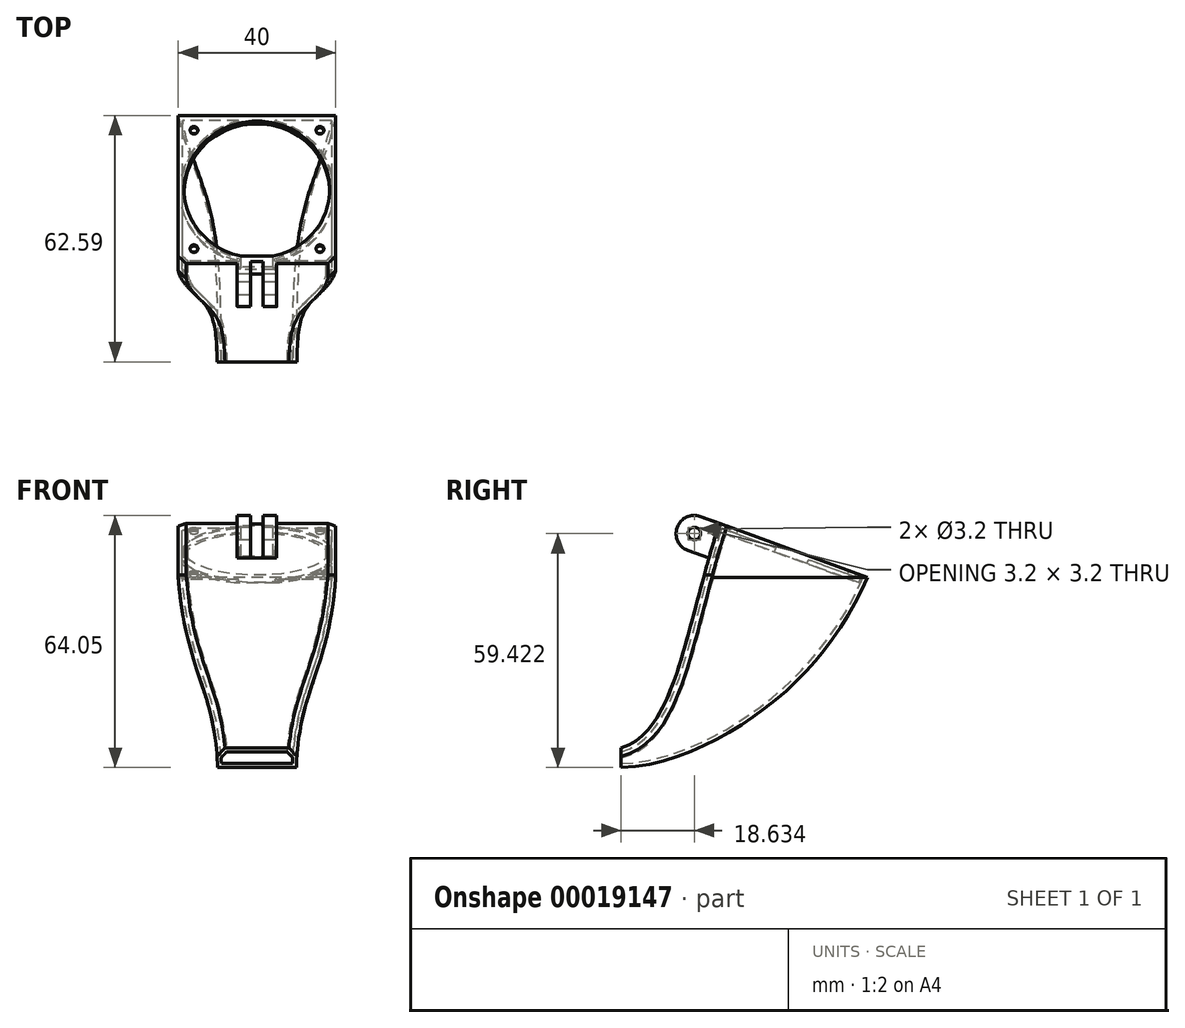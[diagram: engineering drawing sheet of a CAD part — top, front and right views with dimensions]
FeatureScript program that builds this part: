
annotation { "Feature Type Name" : "Feature", "Feature Type Description" : "" }
export const myFeature = defineFeature(function(context is Context, id is Id, definition is map)
    precondition{}
    {
        {
            var Q0;
            Q0=qCreatedBy(makeId("Right.planeOp"),FACE);
            var sketch = newSketch(context, id + "F0", { "sketchPlane" : qUnion([Q0])});
            skLineSegment(sketch, "E0", {"start": v(0, 5) * mm, "end": v(0, 0) * mm});
            skLineSegment(sketch, "E1", {"start": v(62.59, 48.32) * mm, "end": v(25, 62) * mm});
            skFitSpline(sketch, "E2", {"points": [v(62.59, 48.32) * mm, v(0, 0) * mm], "startDerivative": vector(-40.57, -96.87) * mm, "endDerivative": vector(-50.06, 0) * mm});
            skFitSpline(sketch, "E3", {"points": [v(25, 62) * mm, v(0, 5) * mm], "startDerivative": vector(-26.25, -81.63) * mm, "endDerivative": vector(-41.59, -11.88) * mm});
            skSolve(sketch);
        }
        {
            var Q0;
            Q0=qSketchRegion(id+"F0",true);
            extrude(context, id + "F1", {"entities" : qUnion([Q0]), "endBound" : BoundingType.SYMMETRIC, "depth" : 40 * mm});
        }
        {
            var Q0;
            Q0=qCreatedBy(makeId("Front.planeOp"),FACE);
            var sketch = newSketch(context, id + "F2", { "sketchPlane" : qUnion([Q0])});
            skLineSegment(sketch, "E4", {"start": v(10, 0) * mm, "end": v(-10, 0) * mm});
            skLineSegment(sketch, "E5", {"start": v(20, 62) * mm, "end": v(-20, 62) * mm});
            skLineSegment(sketch, "E6", {"start": v(-20, 62) * mm, "end": v(-20, 48.32) * mm});
            skLineSegment(sketch, "E7", {"start": v(20, 62) * mm, "end": v(20, 48.32) * mm});
            skPoint(sketch, "E8", {"position": v(0, 0) * mm});
            skFitSpline(sketch, "E9", {"points": [v(20, 48.32) * mm, v(10, 0) * mm], "startDerivative": vector(-5.16, -71.52) * mm, "endDerivative": vector(-1.89, -60.47) * mm});
            skFitSpline(sketch, "E10.0.MirrorCS", {"points": [v(-20, 48.32) * mm, v(-10, 0) * mm], "startDerivative": vector(5.16, -71.52) * mm, "endDerivative": vector(1.89, -60.47) * mm});
            skSolve(sketch);
        }
        {
            var Q0;
            Q0=qSketchRegion(id+"F2",true);
            var Q1;
            Q1=makeQuery(id+"F1.opExtrude","SWEPT_FACE",FACE,{"disambiguationData":[OSD([sQuery(id+"F0.wireOp",EDGE,"E2")])]});
            extrude(context, id + "F3", {"entities" : qUnion([Q0]), "operationType" : NewBodyOperationType.INTERSECT, "endBound" : BoundingType.UP_TO_BODY, "oppositeDirection" : true, "endBoundEntityBody" : qUnion([Q1]), "depth" : 25 * mm});
        }
        {
            var Q0;
            Q0=makeQuery(id+"F1.opExtrude","SWEPT_FACE",FACE,{"disambiguationData":[OSD([sQuery(id+"F0.wireOp",EDGE,"E1")])]});
            var sketch = newSketch(context, id + "F4", { "sketchPlane" : qUnion([Q0])});
            skLineSegment(sketch, "E11", {"start": v(20, 2.29) * mm, "end": v(-20, 42.29) * mm, "construction": true});
            skLineSegment(sketch, "E12", {"start": v(-20, 2.29) * mm, "end": v(20, 42.29) * mm, "construction": true});
            skCircle(sketch, "E13", {"center": v(0, 22.29) * mm, "radius": 18.5 * mm});
            skSolve(sketch);
        }
        {
            var Q0;
            Q0=qSketchRegion(id+"F4",true);
            extrude(context, id + "F5", {"entities" : qUnion([Q0]), "operationType" : NewBodyOperationType.REMOVE, "oppositeDirection" : true, "depth" : 2 * mm});
        }
        {
            var Q0;
            Q0=makeQuery(id+"F3.boolean.opBoolean","COPY",EDGE,{"derivedFrom":makeQuery(id+"F3.opExtrude","TWEAK_EDGE",EDGE,{"derivedFrom":[makeQuery(id+"F1.opExtrude","SWEPT_FACE",FACE,{"disambiguationData":[OSD([sQuery(id+"F0.wireOp",EDGE,"E2")])]}),makeQuery(id+"F2.imprint","IMPRINT",EDGE,{"derivedFrom":sQuery(id+"F2.wireOp",EDGE,"E9")})]})});
            var Q1;
            Q1=makeQuery(id+"F3.boolean.opBoolean","INTERSECT",EDGE,{"derivedFrom":[makeQuery(id+"F1.opExtrude","SWEPT_FACE",FACE,{"disambiguationData":[OSD([sQuery(id+"F0.wireOp",EDGE,"E3")])]}),makeQuery(id+"F3.opExtrude","SWEPT_FACE",FACE,{"disambiguationData":[OSD([sQuery(id+"F2.wireOp",EDGE,"E9")])]})]});
            var Q2;
            Q2=makeQuery(id+"F1.opExtrude","CAP_EDGE",EDGE,{"disambiguationData":[OSD([sQuery(id+"F0.wireOp",EDGE,"E3")])],"isStart":false});
            var Q3;
            Q3=makeQuery(id+"F3.boolean.opBoolean","INTERSECT",EDGE,{"derivedFrom":[makeQuery(id+"F1.opExtrude","SWEPT_FACE",FACE,{"disambiguationData":[OSD([sQuery(id+"F0.wireOp",EDGE,"E3")])]}),makeQuery(id+"F3.opExtrude","SWEPT_FACE",FACE,{"disambiguationData":[OSD([sQuery(id+"F2.wireOp",EDGE,"E10.0.MirrorCS")])]})]});
            var Q4;
            Q4=makeQuery(id+"F1.opExtrude","CAP_EDGE",EDGE,{"disambiguationData":[OSD([sQuery(id+"F0.wireOp",EDGE,"E3")])],"isStart":true});
            var Q5;
            Q5=makeQuery(id+"F3.boolean.opBoolean","COPY",EDGE,{"derivedFrom":makeQuery(id+"F3.opExtrude","TWEAK_EDGE",EDGE,{"derivedFrom":[makeQuery(id+"F1.opExtrude","SWEPT_FACE",FACE,{"disambiguationData":[OSD([sQuery(id+"F0.wireOp",EDGE,"E2")])]}),makeQuery(id+"F2.imprint","IMPRINT",EDGE,{"derivedFrom":sQuery(id+"F2.wireOp",EDGE,"E10.0.MirrorCS")})]})});
            chamfer(context, id + "F6", {"entities" : qUnion([Q0, Q1, Q2, Q3, Q4, Q5]), "width" : 2 * mm, "tangentPropagation" : true});
        }
        {
            var Q0;
            Q0=makeQuery(id+"F5.boolean.opBoolean","COPY",FACE,{"derivedFrom":makeQuery(id+"F5.opExtrude","CAP_FACE",FACE,{"disambiguationData":[OSD([sQuery(id+"F4.wireOp",EDGE,"E13")])],"isStart":false})});
            var Q1;
            Q1=makeQuery(id+"F1.opExtrude","SWEPT_FACE",FACE,{"disambiguationData":[OSD([sQuery(id+"F0.wireOp",EDGE,"E0")])]});
            shell(context, id + "F7", {"entities" : qUnion([Q0, Q1]), "thickness" : 1 * mm});
        }
        {
            var Q0;
            Q0=makeQuery(id+"F1.opExtrude","SWEPT_FACE",FACE,{"disambiguationData":[OSD([sQuery(id+"F0.wireOp",EDGE,"E1")])]});
            var sketch = newSketch(context, id + "F8", { "sketchPlane" : qUnion([Q0])});
            skCircle(sketch, "E14", {"center": v(16, 38.34) * mm, "radius": 1 * mm});
            skCircle(sketch, "E15", {"center": v(-16, 38.34) * mm, "radius": 1 * mm});
            skCircle(sketch, "E16", {"center": v(-16, 6.34) * mm, "radius": 1 * mm});
            skCircle(sketch, "E17", {"center": v(16, 6.34) * mm, "radius": 1 * mm});
            skPoint(sketch, "E18", {"position": v(-20, 22.34) * mm});
            skSolve(sketch);
        }
        {
            var Q0;
            Q0=qSketchRegion(id+"F8",true);
            var Q1;
            Q1=makeQuery(id+"F7.opShell","OFFSET_FACE",FACE,{"disambiguationData":[OSD([sQuery(id+"F0.wireOp",EDGE,"E1")]),OD(1.0)]});
            extrude(context, id + "F9", {"entities" : qUnion([Q0]), "operationType" : NewBodyOperationType.REMOVE, "endBound" : BoundingType.UP_TO_SURFACE, "oppositeDirection" : true, "endBoundEntityFace" : qUnion([Q1]), "depth" : 25 * mm});
        }
        {
            var Q0;
            Q0=qCreatedBy(makeId("Right.planeOp"),FACE);
            var sketch = newSketch(context, id + "F10", { "sketchPlane" : qUnion([Q0])});
            skLineSegment(sketch, "E19", {"start": v(15.88, 65.32) * mm, "end": v(12.74, 56.67) * mm});
            skLineSegment(sketch, "E20", {"start": v(12.74, 56.67) * mm, "end": v(23.73, 52.67) * mm});
            skLineSegment(sketch, "E21", {"start": v(23.73, 52.67) * mm, "end": v(26.88, 61.32) * mm});
            skLineSegment(sketch, "E22", {"start": v(26.88, 61.32) * mm, "end": v(25, 62) * mm});
            skLineSegment(sketch, "E23", {"start": v(25, 62) * mm, "end": v(25, 62) * mm});
            skLineSegment(sketch, "E24", {"start": v(25, 62) * mm, "end": v(15.88, 65.32) * mm});
            skCircle(sketch, "E25", {"center": v(18.63, 59.42) * mm, "radius": 1.6 * mm});
            skSolve(sketch);
        }
        {
            var Q0;
            Q0=qSketchRegion(id+"F10",true);
            extrude(context, id + "F11", {"entities" : qUnion([Q0]), "operationType" : NewBodyOperationType.ADD, "endBound" : BoundingType.SYMMETRIC, "depth" : 10 * mm});
        }
        {
            var Q0;
            Q0=makeQuery(id+"F11.opExtrude","CAP_EDGE",EDGE,{"disambiguationData":[OSD([sQuery(id+"F10.wireOp",EDGE,"E21")])],"isStart":true});
            var Q1;
            Q1=makeQuery(id+"F11.opExtrude","CAP_EDGE",EDGE,{"disambiguationData":[OSD([sQuery(id+"F10.wireOp",EDGE,"E21")])],"isStart":false});
            var Q2;
            Q2=makeQuery(id+"F11.opExtrude","SWEPT_EDGE",EDGE,{"disambiguationData":[OSD([sQuery(id+"F10.wireOp",EDGE,"E20"),sQuery(id+"F10.wireOp",EDGE,"E21")])]});
            chamfer(context, id + "F12", {"entities" : qUnion([Q0, Q1, Q2]), "width" : 1 * mm, "tangentPropagation" : true});
        }
        {
            var Q0;
            Q0=makeQuery(id+"F11.opExtrude","SWEPT_EDGE",EDGE,{"disambiguationData":[OSD([sQuery(id+"F10.wireOp",EDGE,"E19"),sQuery(id+"F10.wireOp",EDGE,"E20")])]});
            var Q1;
            Q1=makeQuery(id+"F11.opExtrude","SWEPT_EDGE",EDGE,{"disambiguationData":[OSD([sQuery(id+"F10.wireOp",EDGE,"E19"),sQuery(id+"F10.wireOp",EDGE,"E24")])]});
            fillet(context, id + "F13", {"entities" : qUnion([Q0, Q1]), "radius" : 4.5 * mm, "tangentPropagation" : true, "allowEdgeOverflow" : false});
        }
        {
            var Q0;
            {var subQ0=sQuery(id+"F10.wireOp",EDGE,"E20");Q0=makeQuery(id+"F11.boolean.opBoolean","SPLIT",FACE,{"disambiguationData":[TD([makeQuery(id+"F1.opExtrude","SWEPT_FACE",FACE,{"disambiguationData":[OSD([sQuery(id+"F0.wireOp",EDGE,"E3")])]})])],"derivedFrom":makeQuery(id+"F11.opExtrude","SWEPT_FACE",FACE,{"disambiguationData":[OSD([subQ0])]})});}
            var sketch = newSketch(context, id + "F14", { "sketchPlane" : qUnion([Q0])});
            skLineSegment(sketch, "E26.bottom", {"start": v(1.6, 20.97) * mm, "end": v(-1.6, 20.97) * mm});
            skLineSegment(sketch, "E26.top", {"start": v(1.6, -2.8) * mm, "end": v(-1.6, -2.8) * mm});
            skLineSegment(sketch, "E26.left", {"start": v(1.6, 20.97) * mm, "end": v(1.6, -2.8) * mm});
            skLineSegment(sketch, "E26.right", {"start": v(-1.6, 20.97) * mm, "end": v(-1.6, -2.8) * mm});
            skPoint(sketch, "E27", {"position": v(0, 20.97) * mm});
            skSolve(sketch);
        }
        {
            var Q0;
            Q0=qSketchRegion(id+"F14",true);
            var Q1;
            Q1=makeQuery(id+"F11.boolean.opBoolean","MERGE",FACE,{"derivedFrom":[makeQuery(id+"F1.opExtrude","SWEPT_FACE",FACE,{"disambiguationData":[OSD([sQuery(id+"F0.wireOp",EDGE,"E1")])]}),makeQuery(id+"F11.opExtrude","SWEPT_FACE",FACE,{"disambiguationData":[OSD([sQuery(id+"F10.wireOp",EDGE,"E22"),sQuery(id+"F10.wireOp",EDGE,"E24")])]})]});
            extrude(context, id + "F15", {"entities" : qUnion([Q0]), "operationType" : NewBodyOperationType.REMOVE, "endBound" : BoundingType.UP_TO_SURFACE, "oppositeDirection" : true, "endBoundEntityFace" : qUnion([Q1]), "depth" : 25 * mm});
        }
    });
